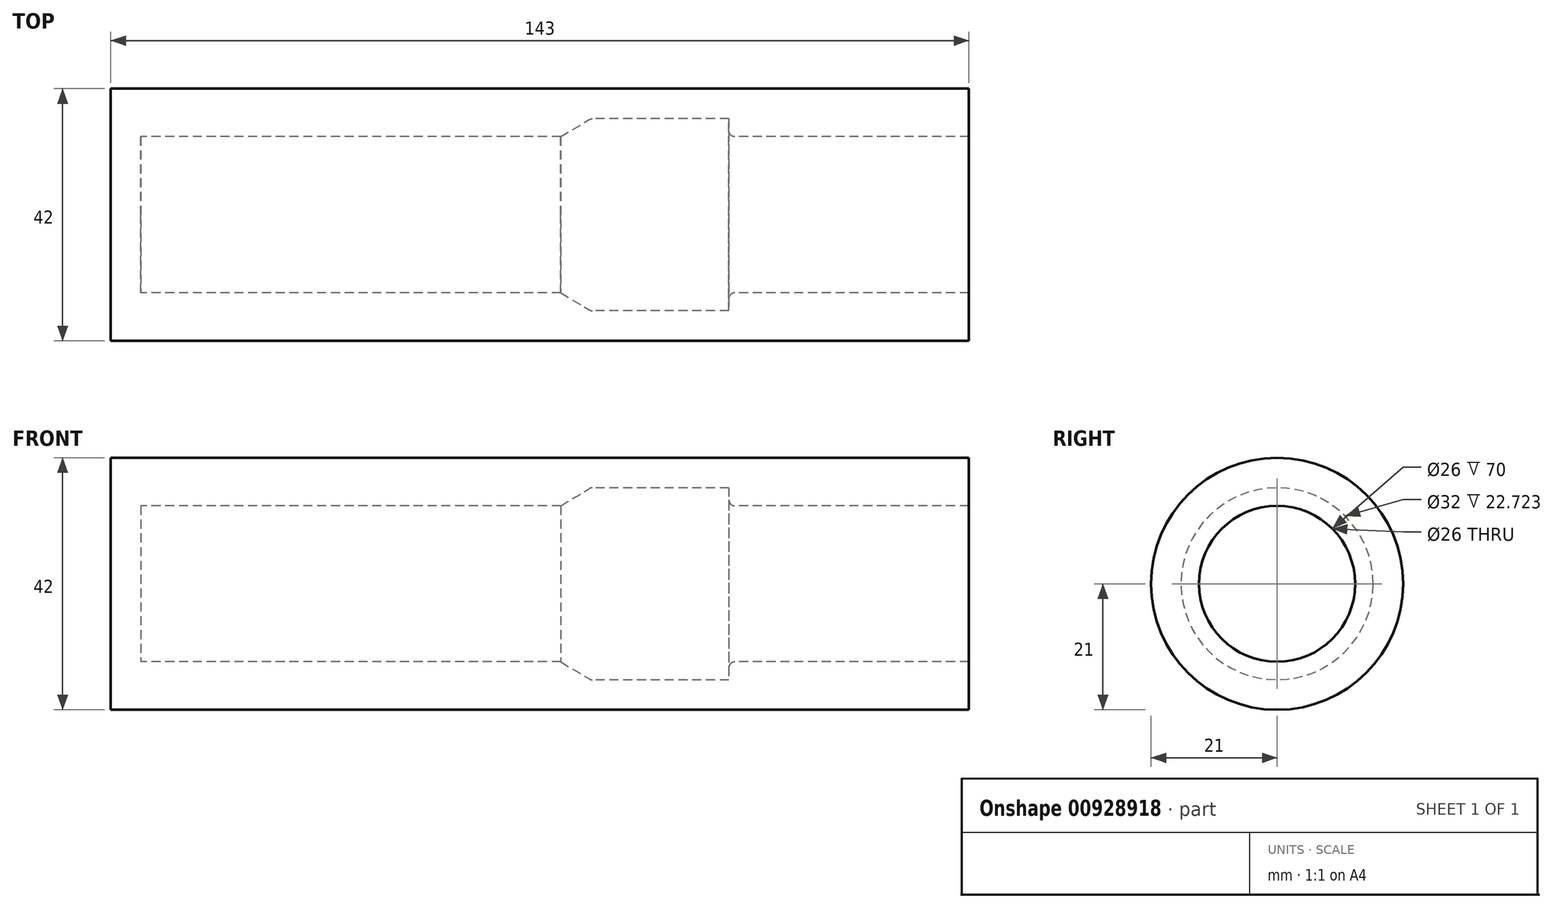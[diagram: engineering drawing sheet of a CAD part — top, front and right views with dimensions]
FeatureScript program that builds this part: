
annotation { "Feature Type Name" : "Feature", "Feature Type Description" : "" }
export const myFeature = defineFeature(function(context is Context, id is Id, definition is map)
    precondition{}
    {
        {
            var Q0;
            Q0=qCreatedBy(makeId("Front.planeOp"),FACE);
            var sketch = newSketch(context, id + "F0", { "sketchPlane" : qUnion([Q0])});
            skLineSegment(sketch, "E0", {"start": v(74.76, 15.86) * mm, "end": v(70, 13) * mm});
            skLineSegment(sketch, "E1", {"start": v(75.28, 16) * mm, "end": v(98, 16) * mm});
            skLineSegment(sketch, "E2", {"start": v(98, 0) * mm, "end": v(70, 0) * mm});
            skPoint(sketch, "E3.visualSharp", {"position": v(75, 16) * mm});
            skArc(sketch, "E3.filletArc", {"start": v(75.28, 16) * mm, "mid": v(75.01, 15.96) * mm, "end": v(74.76, 15.86) * mm});
            skPoint(sketch, "E4.orphan", {"position": v(115, 0) * mm});
            skLineSegment(sketch, "E5", {"start": v(70, 13) * mm, "end": v(0, 13) * mm});
            skLineSegment(sketch, "E6", {"start": v(0, 13) * mm, "end": v(0, 0) * mm});
            skLineSegment(sketch, "E7", {"start": v(0, 0) * mm, "end": v(70, 0) * mm});
            skLineSegment(sketch, "E8", {"start": v(98, 0) * mm, "end": v(138, 0) * mm});
            skLineSegment(sketch, "E9", {"start": v(0, 0) * mm, "end": v(-5, 0) * mm});
            skLineSegment(sketch, "E10", {"start": v(-5, 0) * mm, "end": v(-5, 21) * mm});
            skLineSegment(sketch, "E11", {"start": v(-5, 21) * mm, "end": v(138, 21) * mm});
            skLineSegment(sketch, "E12", {"start": v(98, 16) * mm, "end": v(98, 14) * mm});
            skLineSegment(sketch, "E13", {"start": v(99, 13) * mm, "end": v(138, 13) * mm});
            skPoint(sketch, "E14.visualSharp", {"position": v(98, 13) * mm});
            skArc(sketch, "E14.filletArc", {"start": v(98, 14) * mm, "mid": v(98.3, 13.3) * mm, "end": v(99, 13) * mm});
            skLineSegment(sketch, "E15", {"start": v(138, 13) * mm, "end": v(138, 21) * mm});
            skPoint(sketch, "E16.orphan", {"position": v(133, 21) * mm});
            skSolve(sketch);
        }
        {
            var Q0;
            Q0=makeQuery(id+"F0.imprint","IMPRINT",FACE,{"disambiguationData":[TD([[makeQuery(id+"F0.imprint","IMPRINT",EDGE,{"derivedFrom":sQuery(id+"F0.wireOp",EDGE,"E0")}),-1.0]])]});
            var Q1;
            Q1=sQuery(id+"F0.wireOp",EDGE,"E7");
            revolve(context, id + "F1", {"surfaceOperationType" : NewSurfaceOperationType.NEW, "entities" : qUnion([Q0]), "axis" : qUnion([Q1]), "revolveType" : RevolveType.FULL});
        }
    });
